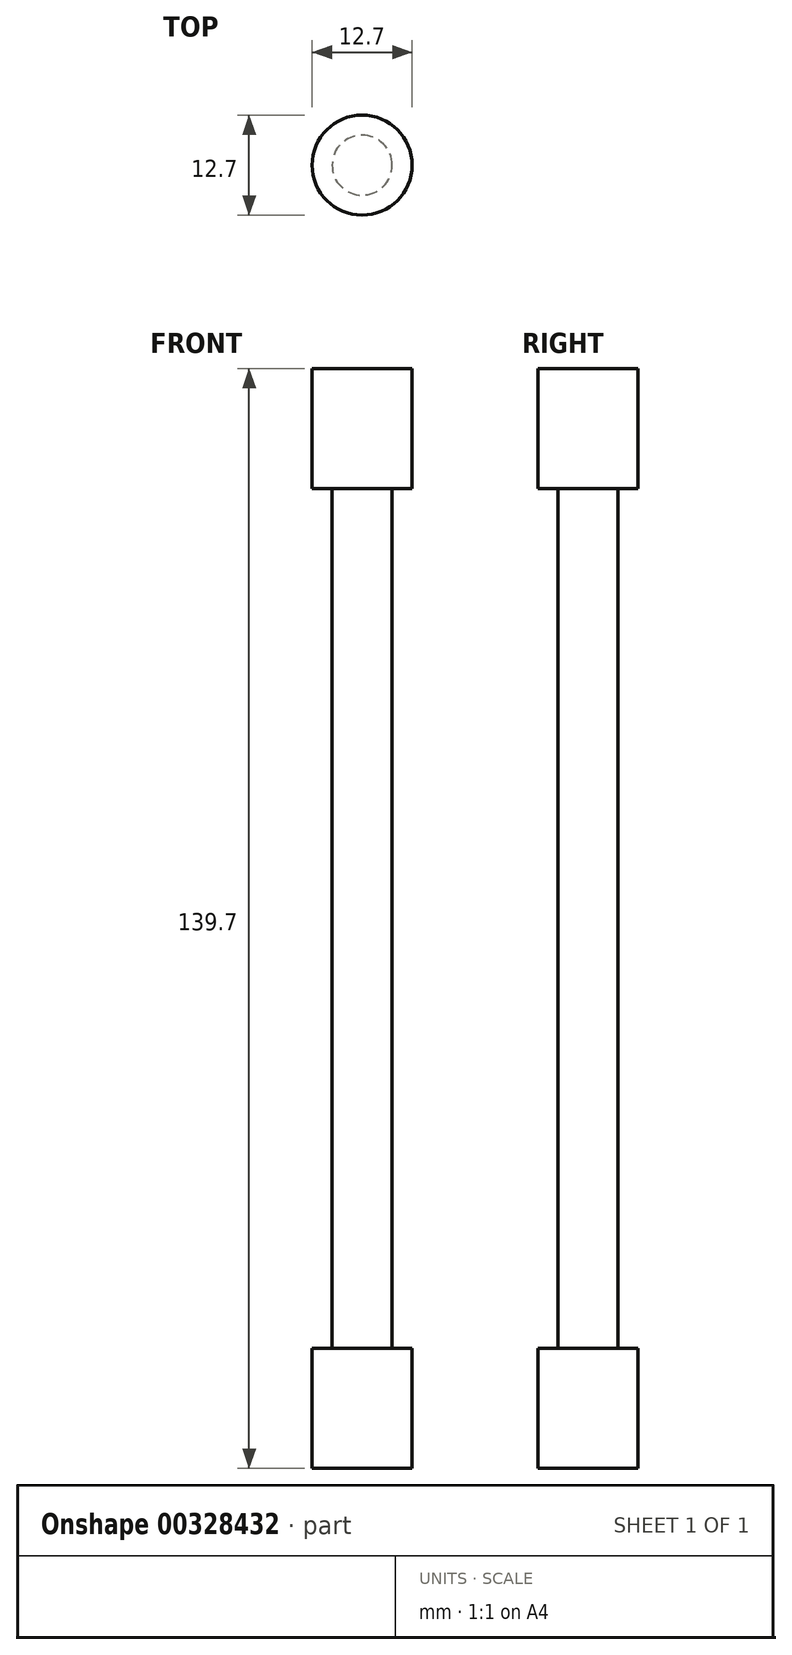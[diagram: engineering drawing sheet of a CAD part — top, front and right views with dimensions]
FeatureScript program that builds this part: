
annotation { "Feature Type Name" : "Feature", "Feature Type Description" : "" }
export const myFeature = defineFeature(function(context is Context, id is Id, definition is map)
    precondition{}
    {
        {
            var Q0;
            Q0=qCreatedBy(makeId("Top.planeOp"),FACE);
            var sketch = newSketch(context, id + "F0", { "sketchPlane" : qUnion([Q0])});
            skCircle(sketch, "E0", {"center": v(0, 0) * mm, "radius": 6.35 * mm});
            skSolve(sketch);
        }
        {
            var Q0;
            Q0=makeQuery(id+"F0.imprint","IMPRINT",FACE,{"disambiguationData":[TD([[makeQuery(id+"F0.imprint","IMPRINT",EDGE,{"derivedFrom":sQuery(id+"F0.wireOp",EDGE,"E0")}),1.0]])]});
            extrude(context, id + "F1", {"entities" : qUnion([Q0]), "depth" : 15.24 * mm});
        }
        {
            var Q0;
            Q0=makeQuery(id+"F1.opExtrude","CAP_FACE",FACE,{"disambiguationData":[OSD([sQuery(id+"F0.wireOp",EDGE,"E0")])],"isStart":false});
            var sketch = newSketch(context, id + "F2", { "sketchPlane" : qUnion([Q0])});
            skCircle(sketch, "E1", {"center": v(0, 0) * mm, "radius": 3.81 * mm});
            skSolve(sketch);
        }
        {
            var Q0;
            Q0=makeQuery(id+"F2.imprint","IMPRINT",FACE,{"disambiguationData":[TD([[makeQuery(id+"F2.imprint","IMPRINT",EDGE,{"derivedFrom":sQuery(id+"F2.wireOp",EDGE,"E1")}),1.0]])]});
            extrude(context, id + "F3", {"entities" : qUnion([Q0]), "operationType" : NewBodyOperationType.ADD, "depth" : 109.22 * mm});
        }
        {
            var Q0;
            Q0=makeQuery(id+"F3.opExtrude","CAP_FACE",FACE,{"disambiguationData":[OSD([sQuery(id+"F2.wireOp",EDGE,"E1")])],"isStart":false});
            var sketch = newSketch(context, id + "F4", { "sketchPlane" : qUnion([Q0])});
            skCircle(sketch, "E2", {"center": v(0, 0) * mm, "radius": 6.35 * mm});
            skSolve(sketch);
        }
        {
            var Q0;
            Q0=makeQuery(id+"F4.imprint","IMPRINT",FACE,{"disambiguationData":[TD([[makeQuery(id+"F4.imprint","IMPRINT",EDGE,{"derivedFrom":sQuery(id+"F4.wireOp",EDGE,"E2")}),1.0]])]});
            var Q1;
            Q1=makeQuery(id+"F4.imprint","IMPRINT",FACE,{"disambiguationData":[TD([[makeQuery(id+"F4.imprint","IMPRINT",EDGE,{"derivedFrom":makeQuery(id+"F3.opExtrude","CAP_EDGE",EDGE,{"disambiguationData":[OSD([sQuery(id+"F2.wireOp",EDGE,"E1")])],"isStart":false})}),1.0]])]});
            extrude(context, id + "F5", {"entities" : qUnion([Q0, Q1]), "operationType" : NewBodyOperationType.ADD, "depth" : 15.24 * mm});
        }
    });
